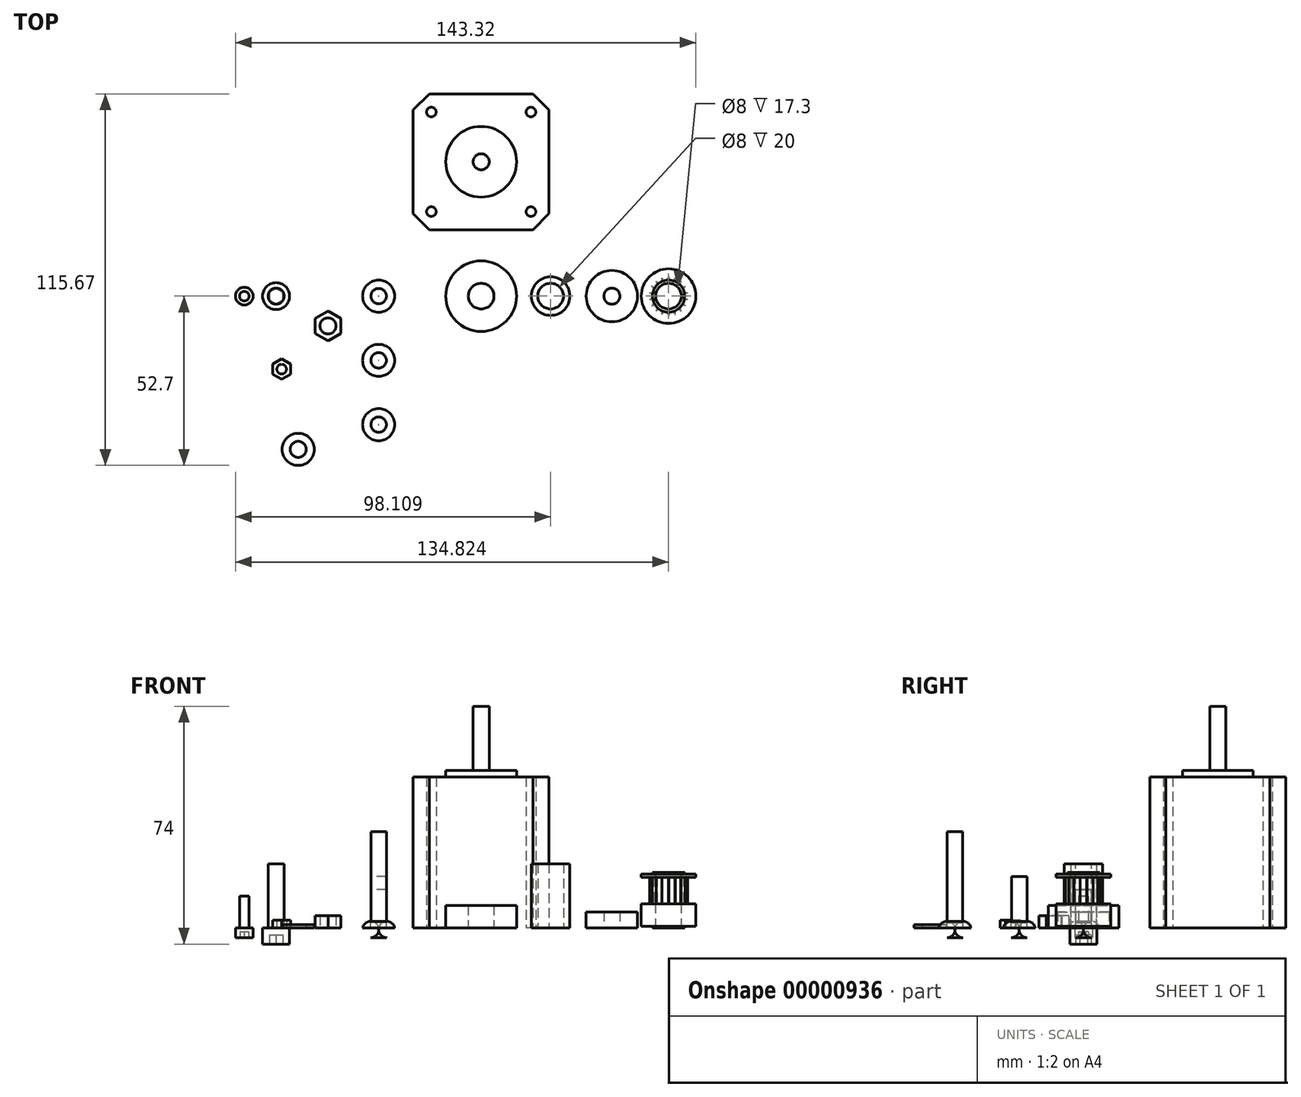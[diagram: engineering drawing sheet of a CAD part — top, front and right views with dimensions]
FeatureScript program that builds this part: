
annotation { "Feature Type Name" : "Feature", "Feature Type Description" : "" }
export const myFeature = defineFeature(function(context is Context, id is Id, definition is map)
    precondition{}
    {
        {
            var Q0;
            Q0=qCreatedBy(makeId("Top.planeOp"),FACE);
            var sketch = newSketch(context, id + "F0", { "sketchPlane" : qUnion([Q0])});
            skCircle(sketch, "E0", {"center": v(0, 0) * mm, "radius": 11 * mm});
            skCircle(sketch, "E1", {"center": v(0, 0) * mm, "radius": 4 * mm});
            skSolve(sketch);
        }
        {
            var Q0;
            Q0=makeQuery(id+"F0.imprint","IMPRINT",FACE,{"disambiguationData":[TD([[makeQuery(id+"F0.imprint","IMPRINT",EDGE,{"derivedFrom":sQuery(id+"F0.wireOp",EDGE,"E0")}),1.0]])]});
            extrude(context, id + "F1", {"entities" : qUnion([Q0]), "depth" : 7 * mm});
        }
        {
            var Q0;
            Q0=qCreatedBy(makeId("Top.planeOp"),FACE);
            var sketch = newSketch(context, id + "F2", { "sketchPlane" : qUnion([Q0])});
            skCircle(sketch, "E2.cCircle", {"center": v(-47.67, -9.27) * mm, "radius": 4 * mm, "construction": true});
            skLineSegment(sketch, "E2.0", {"start": v(-43.67, -6.96) * mm, "end": v(-43.67, -11.58) * mm});
            skLineSegment(sketch, "E2.1", {"start": v(-43.67, -11.58) * mm, "end": v(-47.67, -13.9) * mm});
            skLineSegment(sketch, "E2.2", {"start": v(-47.67, -13.9) * mm, "end": v(-51.67, -11.58) * mm});
            skLineSegment(sketch, "E2.3", {"start": v(-51.67, -11.58) * mm, "end": v(-51.67, -6.96) * mm});
            skLineSegment(sketch, "E2.4", {"start": v(-51.67, -6.96) * mm, "end": v(-47.67, -4.65) * mm});
            skLineSegment(sketch, "E2.5", {"start": v(-47.67, -4.65) * mm, "end": v(-43.67, -6.96) * mm});
            skPoint(sketch, "E2.0.midPoint", {"position": v(-43.67, -9.27) * mm});
            skCircle(sketch, "E3", {"center": v(-47.67, -9.27) * mm, "radius": 2.5 * mm});
            skSolve(sketch);
        }
        {
            var Q0;
            Q0=makeQuery(id+"F2.imprint","IMPRINT",FACE,{"disambiguationData":[TD([[makeQuery(id+"F2.imprint","IMPRINT",EDGE,{"derivedFrom":sQuery(id+"F2.wireOp",EDGE,"E2.0")}),-1.0]])]});
            extrude(context, id + "F3", {"entities" : qUnion([Q0]), "depth" : 3.8 * mm});
        }
        {
            var Q0;
            Q0=qCreatedBy(makeId("Front.planeOp"),FACE);
            var sketch = newSketch(context, id + "F4", { "sketchPlane" : qUnion([Q0])});
            skLineSegment(sketch, "E4", {"start": v(-36.9, 0) * mm, "end": v(-34.4, 0) * mm});
            skLineSegment(sketch, "E5", {"start": v(-34.4, 0) * mm, "end": v(-34.4, 1.7) * mm});
            skLineSegment(sketch, "E6", {"start": v(-34.3, 12) * mm, "end": v(-31.9, 12) * mm});
            skLineSegment(sketch, "E7", {"start": v(-31.9, 12) * mm, "end": v(-31.9, -3) * mm});
            skLineSegment(sketch, "E8", {"start": v(-31.9, -3) * mm, "end": v(-34.4, -3) * mm});
            skArc(sketch, "E9", {"start": v(-36.9, 0) * mm, "mid": v(-36.35, -2.09) * mm, "end": v(-34.4, -3) * mm});
            skLineSegment(sketch, "E10", {"start": v(-34.4, 1.7) * mm, "end": v(-34.3, 1.7) * mm});
            skLineSegment(sketch, "E11", {"start": v(-34.3, 1.7) * mm, "end": v(-34.3, 12) * mm});
            skSolve(sketch);
        }
        {
            var Q0;
            Q0=makeQuery(id+"F4.imprint","IMPRINT",FACE,{"disambiguationData":[TD([[makeQuery(id+"F4.imprint","IMPRINT",EDGE,{"derivedFrom":sQuery(id+"F4.wireOp",EDGE,"E4")}),-1.0]])]});
            var Q1;
            Q1=sQuery(id+"F4.wireOp",EDGE,"E7");
            revolve(context, id + "F5", {"entities" : qUnion([Q0]), "axis" : qUnion([Q1]), "revolveType" : RevolveType.FULL});
        }
        {
            var Q0;
            Q0=makeQuery(id+"F5.opRevolve","SWEPT_BODY",BODY,{"disambiguationData":[OSD([sQuery(id+"F4.wireOp",EDGE,"E4"),sQuery(id+"F4.wireOp",EDGE,"E5"),sQuery(id+"F4.wireOp",EDGE,"E6"),sQuery(id+"F4.wireOp",EDGE,"E7"),sQuery(id+"F4.wireOp",EDGE,"E8"),sQuery(id+"F4.wireOp",EDGE,"E9")])]});
            transform(context, id + "F6", {"entities" : qUnion([Q0]), "transformType" : TransformType.TRANSLATION_3D, "dx" : 0 * mm, "dy" : -(20 * mm), "dz" : 0 * mm, "makeCopy" : true});
        }
        {
            var Q0;
            Q0=makeQuery(id+"F6.opPattern","COPY",FACE,{"derivedFrom":makeQuery(id+"F5.opRevolve","SWEPT_FACE",FACE,{"disambiguationData":[OSD([sQuery(id+"F4.wireOp",EDGE,"E6")])]}),"instanceName":"1"});
            extrude(context, id + "F7", {"entities" : qUnion([Q0]), "operationType" : NewBodyOperationType.ADD, "depth" : 4 * mm});
        }
        {
            var Q0;
            Q0=qCreatedBy(makeId("Front.planeOp"),FACE);
            var sketch = newSketch(context, id + "F8", { "sketchPlane" : qUnion([Q0])});
            skLineSegment(sketch, "E12", {"start": v(-68.03, 0) * mm, "end": v(-66.33, 0) * mm});
            skLineSegment(sketch, "E13", {"start": v(-66.33, 0) * mm, "end": v(-66.33, 20) * mm});
            skLineSegment(sketch, "E14", {"start": v(-66.33, 20) * mm, "end": v(-63.83, 20) * mm});
            skLineSegment(sketch, "E15", {"start": v(-63.83, 20) * mm, "end": v(-63.83, -5) * mm});
            skLineSegment(sketch, "E16", {"start": v(-63.83, -5) * mm, "end": v(-68.03, -5) * mm});
            skLineSegment(sketch, "E17", {"start": v(-68.03, -5) * mm, "end": v(-68.03, 0) * mm});
            skSolve(sketch);
        }
        {
            var Q0;
            Q0=makeQuery(id+"F8.imprint","IMPRINT",FACE,{"disambiguationData":[TD([[makeQuery(id+"F8.imprint","IMPRINT",EDGE,{"derivedFrom":sQuery(id+"F8.wireOp",EDGE,"E12")}),-1.0]])]});
            var Q1;
            Q1=sQuery(id+"F8.wireOp",EDGE,"E15");
            revolve(context, id + "F9", {"entities" : qUnion([Q0]), "axis" : qUnion([Q1]), "revolveType" : RevolveType.FULL});
        }
        {
            var Q0;
            Q0=makeQuery(id+"F9.opRevolve","SWEPT_FACE",FACE,{"disambiguationData":[OSD([sQuery(id+"F8.wireOp",EDGE,"E16")])]});
            var sketch = newSketch(context, id + "F10", { "sketchPlane" : qUnion([Q0])});
            skCircle(sketch, "E18.cCircle", {"center": v(-63.83, 0) * mm, "radius": 2.06 * mm, "construction": true});
            skLineSegment(sketch, "E18.0", {"start": v(-61.77, 1.19) * mm, "end": v(-61.77, -1.19) * mm});
            skLineSegment(sketch, "E18.1", {"start": v(-61.77, -1.19) * mm, "end": v(-63.83, -2.38) * mm});
            skLineSegment(sketch, "E18.2", {"start": v(-63.83, -2.38) * mm, "end": v(-65.89, -1.19) * mm});
            skLineSegment(sketch, "E18.3", {"start": v(-65.89, -1.19) * mm, "end": v(-65.89, 1.19) * mm});
            skLineSegment(sketch, "E18.4", {"start": v(-65.89, 1.19) * mm, "end": v(-63.83, 2.38) * mm});
            skLineSegment(sketch, "E18.5", {"start": v(-63.83, 2.38) * mm, "end": v(-61.77, 1.19) * mm});
            skPoint(sketch, "E18.0.midPoint", {"position": v(-61.77, 0) * mm});
            skSolve(sketch);
        }
        {
            var Q0;
            Q0=makeQuery(id+"F10.imprint","IMPRINT",FACE,{"disambiguationData":[TD([[makeQuery(id+"F10.imprint","IMPRINT",EDGE,{"derivedFrom":sQuery(id+"F10.wireOp",EDGE,"E18.0")}),-1.0]])]});
            extrude(context, id + "F11", {"entities" : qUnion([Q0]), "operationType" : NewBodyOperationType.REMOVE, "oppositeDirection" : true, "depth" : 2.9 * mm});
        }
        {
            var Q0;
            Q0=qCreatedBy(makeId("Top.planeOp"),FACE);
            var sketch = newSketch(context, id + "F12", { "sketchPlane" : qUnion([Q0])});
            skCircle(sketch, "E19", {"center": v(21.62, 0) * mm, "radius": 4 * mm});
            skCircle(sketch, "E20", {"center": v(21.62, 0) * mm, "radius": 6 * mm});
            skSolve(sketch);
        }
        {
            var Q0;
            Q0=makeQuery(id+"F12.imprint","IMPRINT",FACE,{"disambiguationData":[TD([[makeQuery(id+"F12.imprint","IMPRINT",EDGE,{"derivedFrom":sQuery(id+"F12.wireOp",EDGE,"E19")}),-1.0]])]});
            extrude(context, id + "F13", {"entities" : qUnion([Q0]), "depth" : 20 * mm});
        }
        {
            var Q0;
            Q0=qCreatedBy(makeId("Top.planeOp"),FACE);
            var sketch = newSketch(context, id + "F14", { "sketchPlane" : qUnion([Q0])});
            skCircle(sketch, "E21", {"center": v(40.7, 0) * mm, "radius": 2.5 * mm});
            skCircle(sketch, "E22", {"center": v(40.7, 0) * mm, "radius": 8 * mm});
            skSolve(sketch);
        }
        {
            var Q0;
            Q0=makeQuery(id+"F14.imprint","IMPRINT",FACE,{"disambiguationData":[TD([[makeQuery(id+"F14.imprint","IMPRINT",EDGE,{"derivedFrom":sQuery(id+"F14.wireOp",EDGE,"E21")}),-1.0]])]});
            extrude(context, id + "F15", {"entities" : qUnion([Q0]), "depth" : 5 * mm});
        }
        {
            var Q0;
            Q0=qCreatedBy(makeId("Front.planeOp"),FACE);
            var sketch = newSketch(context, id + "F16", { "sketchPlane" : qUnion([Q0])});
            skLineSegment(sketch, "E23", {"start": v(54.33, 0) * mm, "end": v(54.33, 17.3) * mm});
            skLineSegment(sketch, "E24", {"start": v(54.33, 17.3) * mm, "end": v(53.33, 17.3) * mm});
            skLineSegment(sketch, "E25", {"start": v(53.33, 17.3) * mm, "end": v(53.33, 16.8) * mm});
            skLineSegment(sketch, "E26", {"start": v(53.33, 16.8) * mm, "end": v(49.83, 16.8) * mm});
            skLineSegment(sketch, "E27", {"start": v(49.83, 16.8) * mm, "end": v(49.83, 15.8) * mm});
            skLineSegment(sketch, "E28", {"start": v(49.83, 15.8) * mm, "end": v(52.33, 15.8) * mm});
            skLineSegment(sketch, "E29", {"start": v(52.33, 15.8) * mm, "end": v(52.33, 7.5) * mm});
            skLineSegment(sketch, "E30", {"start": v(52.33, 7.5) * mm, "end": v(49.83, 7.5) * mm});
            skLineSegment(sketch, "E31", {"start": v(49.83, 7.5) * mm, "end": v(49.83, 0.5) * mm});
            skLineSegment(sketch, "E32", {"start": v(49.83, 0.5) * mm, "end": v(53.33, 0.5) * mm});
            skLineSegment(sketch, "E33", {"start": v(53.33, 0.5) * mm, "end": v(53.33, 0) * mm});
            skLineSegment(sketch, "E34", {"start": v(53.33, 0) * mm, "end": v(54.33, 0) * mm});
            skLineSegment(sketch, "E35", {"start": v(58.33, 17.3) * mm, "end": v(58.33, 0) * mm, "construction": true});
            skSolve(sketch);
        }
        {
            var Q0;
            Q0=makeQuery(id+"F16.imprint","IMPRINT",FACE,{"disambiguationData":[TD([[makeQuery(id+"F16.imprint","IMPRINT",EDGE,{"derivedFrom":sQuery(id+"F16.wireOp",EDGE,"E23")}),1.0]])]});
            var Q1;
            Q1=sQuery(id+"F16.wireOp",EDGE,"E35");
            revolve(context, id + "F17", {"entities" : qUnion([Q0]), "axis" : qUnion([Q1]), "revolveType" : RevolveType.FULL});
        }
        {
            var Q0;
            Q0=qCreatedBy(makeId("Top.planeOp"),FACE);
            var sketch = newSketch(context, id + "F18", { "sketchPlane" : qUnion([Q0])});
            skLineSegment(sketch, "E36.rect.bottom", {"start": v(21.15, 20.67) * mm, "end": v(-21.15, 20.67) * mm});
            skLineSegment(sketch, "E36.rect.top", {"start": v(21.15, 62.97) * mm, "end": v(-21.15, 62.97) * mm});
            skLineSegment(sketch, "E36.rect.left", {"start": v(21.15, 20.67) * mm, "end": v(21.15, 62.97) * mm});
            skLineSegment(sketch, "E36.rect.right", {"start": v(-21.15, 20.67) * mm, "end": v(-21.15, 62.97) * mm});
            skPoint(sketch, "E36.rect.middle", {"position": v(0, 41.82) * mm});
            skCircle(sketch, "E37", {"center": v(0, 41.82) * mm, "radius": 11 * mm});
            skCircle(sketch, "E38", {"center": v(0, 41.82) * mm, "radius": 2.5 * mm});
            skLineSegment(sketch, "E39", {"start": v(-21.15, 57.97) * mm, "end": v(-16.15, 62.97) * mm});
            skLineSegment(sketch, "E40", {"start": v(16.15, 62.97) * mm, "end": v(21.15, 57.97) * mm});
            skLineSegment(sketch, "E41", {"start": v(21.15, 25.67) * mm, "end": v(16.15, 20.67) * mm});
            skLineSegment(sketch, "E42", {"start": v(-21.15, 25.67) * mm, "end": v(-16.15, 20.67) * mm});
            skLineSegment(sketch, "E43.rect.bottom", {"start": v(15.5, 57.32) * mm, "end": v(-15.5, 57.32) * mm, "construction": true});
            skLineSegment(sketch, "E43.rect.top", {"start": v(15.5, 26.32) * mm, "end": v(-15.5, 26.32) * mm, "construction": true});
            skLineSegment(sketch, "E43.rect.left", {"start": v(15.5, 57.32) * mm, "end": v(15.5, 26.32) * mm, "construction": true});
            skLineSegment(sketch, "E43.rect.right", {"start": v(-15.5, 57.32) * mm, "end": v(-15.5, 26.32) * mm, "construction": true});
            skCircle(sketch, "E44", {"center": v(-15.5, 57.32) * mm, "radius": 1.5 * mm});
            skCircle(sketch, "E45", {"center": v(15.5, 57.32) * mm, "radius": 1.5 * mm});
            skCircle(sketch, "E46", {"center": v(15.5, 26.32) * mm, "radius": 1.5 * mm});
            skCircle(sketch, "E47", {"center": v(-15.5, 26.32) * mm, "radius": 1.5 * mm});
            skSolve(sketch);
        }
        {
            var Q0;
            Q0=makeQuery(id+"F18.imprint","IMPRINT",FACE,{"disambiguationData":[TD([[makeQuery(id+"F18.imprint","IMPRINT",EDGE,{"derivedFrom":sQuery(id+"F18.wireOp",EDGE,"E37")}),-1.0]])]});
            extrude(context, id + "F19", {"entities" : qUnion([Q0]), "depth" : 47 * mm});
        }
        {
            var Q0;
            Q0=makeQuery(id+"F18.imprint","IMPRINT",FACE,{"disambiguationData":[TD([[makeQuery(id+"F18.imprint","IMPRINT",EDGE,{"derivedFrom":sQuery(id+"F18.wireOp",EDGE,"E37")}),1.0]])]});
            extrude(context, id + "F20", {"entities" : qUnion([Q0]), "operationType" : NewBodyOperationType.ADD, "depth" : 49 * mm});
        }
        {
            var Q0;
            Q0=makeQuery(id+"F18.imprint","IMPRINT",FACE,{"disambiguationData":[TD([[makeQuery(id+"F18.imprint","IMPRINT",EDGE,{"derivedFrom":sQuery(id+"F18.wireOp",EDGE,"E38")}),1.0]])]});
            extrude(context, id + "F21", {"entities" : qUnion([Q0]), "operationType" : NewBodyOperationType.ADD, "depth" : 69 * mm});
        }
        {
            var Q0;
            Q0=qCreatedBy(makeId("Top.planeOp"),FACE);
            var sketch = newSketch(context, id + "F22", { "sketchPlane" : qUnion([Q0])});
            skCircle(sketch, "E48", {"center": v(-62.1, -22.71) * mm, "radius": 1.5 * mm});
            skCircle(sketch, "E49.cCircle", {"center": v(-62.1, -22.71) * mm, "radius": 2.75 * mm, "construction": true});
            skLineSegment(sketch, "E49.0", {"start": v(-59.35, -21.12) * mm, "end": v(-59.35, -24.3) * mm});
            skLineSegment(sketch, "E49.1", {"start": v(-59.35, -24.3) * mm, "end": v(-62.1, -25.89) * mm});
            skLineSegment(sketch, "E49.2", {"start": v(-62.1, -25.89) * mm, "end": v(-64.85, -24.3) * mm});
            skLineSegment(sketch, "E49.3", {"start": v(-64.85, -24.3) * mm, "end": v(-64.85, -21.12) * mm});
            skLineSegment(sketch, "E49.4", {"start": v(-64.85, -21.12) * mm, "end": v(-62.1, -19.54) * mm});
            skLineSegment(sketch, "E49.5", {"start": v(-62.1, -19.54) * mm, "end": v(-59.35, -21.12) * mm});
            skPoint(sketch, "E49.0.midPoint", {"position": v(-59.35, -22.71) * mm});
            skSolve(sketch);
        }
        {
            var Q0;
            Q0=makeQuery(id+"F22.imprint","IMPRINT",FACE,{"disambiguationData":[TD([[makeQuery(id+"F22.imprint","IMPRINT",EDGE,{"derivedFrom":sQuery(id+"F22.wireOp",EDGE,"E48")}),-1.0]])]});
            extrude(context, id + "F23", {"entities" : qUnion([Q0]), "depth" : 2.4 * mm});
        }
        {
            var Q0;
            Q0=qCreatedBy(makeId("Front.planeOp"),FACE);
            var sketch = newSketch(context, id + "F24", { "sketchPlane" : qUnion([Q0])});
            skLineSegment(sketch, "E50", {"start": v(-75.24, 0) * mm, "end": v(-76.49, 0) * mm});
            skLineSegment(sketch, "E51", {"start": v(-76.49, 0) * mm, "end": v(-76.49, -3) * mm});
            skLineSegment(sketch, "E52", {"start": v(-76.49, -3) * mm, "end": v(-73.74, -3) * mm});
            skLineSegment(sketch, "E53", {"start": v(-73.74, -3) * mm, "end": v(-73.74, 10) * mm});
            skLineSegment(sketch, "E54", {"start": v(-73.74, 10) * mm, "end": v(-75.24, 10) * mm});
            skLineSegment(sketch, "E55", {"start": v(-75.24, 10) * mm, "end": v(-75.24, 0) * mm});
            skSolve(sketch);
        }
        {
            var Q0;
            Q0=makeQuery(id+"F24.imprint","IMPRINT",FACE,{"disambiguationData":[TD([[makeQuery(id+"F24.imprint","IMPRINT",EDGE,{"derivedFrom":sQuery(id+"F24.wireOp",EDGE,"E50")}),1.0]])]});
            var Q1;
            Q1=sQuery(id+"F24.wireOp",EDGE,"E53");
            revolve(context, id + "F25", {"entities" : qUnion([Q0]), "axis" : qUnion([Q1]), "revolveType" : RevolveType.FULL});
        }
        {
            var Q0;
            Q0=makeQuery(id+"F25.opRevolve","SWEPT_FACE",FACE,{"disambiguationData":[OSD([sQuery(id+"F24.wireOp",EDGE,"E52")])]});
            var sketch = newSketch(context, id + "F26", { "sketchPlane" : qUnion([Q0])});
            skCircle(sketch, "E56.cCircle", {"center": v(-73.74, 0) * mm, "radius": 1.3 * mm, "construction": true});
            skLineSegment(sketch, "E56.0", {"start": v(-72.44, 0.75) * mm, "end": v(-72.44, -0.75) * mm});
            skLineSegment(sketch, "E56.1", {"start": v(-72.44, -0.75) * mm, "end": v(-73.74, -1.5) * mm});
            skLineSegment(sketch, "E56.2", {"start": v(-73.74, -1.5) * mm, "end": v(-75.04, -0.75) * mm});
            skLineSegment(sketch, "E56.3", {"start": v(-75.04, -0.75) * mm, "end": v(-75.04, 0.75) * mm});
            skLineSegment(sketch, "E56.4", {"start": v(-75.04, 0.75) * mm, "end": v(-73.74, 1.5) * mm});
            skLineSegment(sketch, "E56.5", {"start": v(-73.74, 1.5) * mm, "end": v(-72.44, 0.75) * mm});
            skPoint(sketch, "E56.0.midPoint", {"position": v(-72.44, 0) * mm});
            skSolve(sketch);
        }
        {
            var Q0;
            Q0=makeQuery(id+"F26.imprint","IMPRINT",FACE,{"disambiguationData":[TD([[makeQuery(id+"F26.imprint","IMPRINT",EDGE,{"derivedFrom":sQuery(id+"F26.wireOp",EDGE,"E56.0")}),-1.0]])]});
            extrude(context, id + "F27", {"entities" : qUnion([Q0]), "operationType" : NewBodyOperationType.REMOVE, "oppositeDirection" : true, "depth" : 1.9 * mm});
        }
        {
            var Q0;
            Q0=makeQuery(id+"F17.opRevolve","SWEPT_FACE",FACE,{"disambiguationData":[OSD([sQuery(id+"F16.wireOp",EDGE,"E30")])]});
            var sketch = newSketch(context, id + "F28", { "sketchPlane" : qUnion([Q0])});
            skLineSegment(sketch, "E57.0", {"start": v(64.16, -0.98) * mm, "end": v(64.15, -1.07) * mm});
            skLineSegment(sketch, "E57.1", {"start": v(63.47, -2.92) * mm, "end": v(63.43, -3) * mm});
            skLineSegment(sketch, "E57.2", {"start": v(62.16, -4.5) * mm, "end": v(62.1, -4.55) * mm});
            skLineSegment(sketch, "E57.3", {"start": v(60.4, -5.54) * mm, "end": v(60.32, -5.57) * mm});
            skLineSegment(sketch, "E57.4", {"start": v(58.38, -5.9) * mm, "end": v(58.3, -5.9) * mm});
            skLineSegment(sketch, "E57.5", {"start": v(56.35, -5.57) * mm, "end": v(56.27, -5.54) * mm});
            skLineSegment(sketch, "E57.6", {"start": v(54.57, -4.55) * mm, "end": v(54.5, -4.5) * mm});
            skLineSegment(sketch, "E57.7", {"start": v(53.24, -3) * mm, "end": v(53.2, -2.92) * mm});
            skLineSegment(sketch, "E57.8", {"start": v(52.52, -1.07) * mm, "end": v(52.5, -0.98) * mm});
            skLineSegment(sketch, "E57.9", {"start": v(52.5, 0.98) * mm, "end": v(52.52, 1.07) * mm});
            skLineSegment(sketch, "E57.10", {"start": v(53.2, 2.92) * mm, "end": v(53.24, 3) * mm});
            skLineSegment(sketch, "E57.11", {"start": v(54.5, 4.5) * mm, "end": v(54.57, 4.55) * mm});
            skLineSegment(sketch, "E57.12", {"start": v(56.27, 5.54) * mm, "end": v(56.35, 5.57) * mm});
            skLineSegment(sketch, "E57.13", {"start": v(58.3, 5.9) * mm, "end": v(58.38, 5.9) * mm});
            skLineSegment(sketch, "E57.14", {"start": v(60.32, 5.57) * mm, "end": v(60.4, 5.54) * mm});
            skLineSegment(sketch, "E57.15", {"start": v(62.1, 4.55) * mm, "end": v(62.16, 4.5) * mm});
            skLineSegment(sketch, "E57.16", {"start": v(63.43, 3) * mm, "end": v(63.47, 2.92) * mm});
            skLineSegment(sketch, "E57.17", {"start": v(64.15, 1.07) * mm, "end": v(64.16, 0.98) * mm});
            skCircle(sketch, "E58", {"center": v(55.33, -5.2) * mm, "radius": 1 * mm});
            skCircle(sketch, "E59", {"center": v(53.74, -3.86) * mm, "radius": 1 * mm});
            skCircle(sketch, "E60", {"center": v(52.7, -2.05) * mm, "radius": 1 * mm});
            skCircle(sketch, "E61", {"center": v(52.33, 0) * mm, "radius": 1 * mm});
            skCircle(sketch, "E62", {"center": v(52.7, 2.05) * mm, "radius": 1 * mm});
            skCircle(sketch, "E63", {"center": v(57.3, -5.9) * mm, "radius": 1 * mm});
            skCircle(sketch, "E64", {"center": v(59.38, -5.9) * mm, "radius": 1 * mm});
            skCircle(sketch, "E65", {"center": v(61.33, -5.2) * mm, "radius": 1 * mm});
            skCircle(sketch, "E66", {"center": v(62.93, -3.86) * mm, "radius": 1 * mm});
            skCircle(sketch, "E67", {"center": v(63.97, -2.05) * mm, "radius": 1 * mm});
            skCircle(sketch, "E68", {"center": v(64.33, 0) * mm, "radius": 1 * mm});
            skCircle(sketch, "E69", {"center": v(63.97, 2.05) * mm, "radius": 1 * mm});
            skCircle(sketch, "E70", {"center": v(62.93, 3.86) * mm, "radius": 1 * mm});
            skCircle(sketch, "E71", {"center": v(61.33, 5.2) * mm, "radius": 1 * mm});
            skCircle(sketch, "E72", {"center": v(59.38, 5.9) * mm, "radius": 1 * mm});
            skCircle(sketch, "E73", {"center": v(57.3, 5.9) * mm, "radius": 1 * mm});
            skCircle(sketch, "E74", {"center": v(55.33, 5.2) * mm, "radius": 1 * mm});
            skCircle(sketch, "E75", {"center": v(53.74, 3.86) * mm, "radius": 1 * mm});
            skSolve(sketch);
        }
        {
            var Q0;
            {var subQ0=sQuery(id+"F28.wireOp",EDGE,"E62");var subQ2=makeQuery(id+"F28.imprint","INTERSECT",VERTEX,{"derivedFrom":[sQuery(id+"F28.wireOp",EDGE,"E57.9"),subQ0]});Q0=makeQuery(id+"F28.imprint","IMPRINT",FACE,{"disambiguationData":[TD([[makeQuery(id+"F28.imprint","IMPRINT",EDGE,{"disambiguationData":[TD([[subQ2,-1.0]])],"derivedFrom":subQ0}),1.0]])]});}
            var Q1;
            {var subQ1=sQuery(id+"F28.wireOp",EDGE,"E61");var subQ5=makeQuery(id+"F28.imprint","INTERSECT",VERTEX,{"derivedFrom":[sQuery(id+"F28.wireOp",EDGE,"E57.8"),subQ1]});Q1=makeQuery(id+"F28.imprint","IMPRINT",FACE,{"disambiguationData":[TD([[makeQuery(id+"F28.imprint","IMPRINT",EDGE,{"disambiguationData":[TD([[subQ5,-1.0]])],"derivedFrom":subQ1}),1.0]])]});}
            var Q2;
            {var subQ1=sQuery(id+"F28.wireOp",EDGE,"E60");var subQ5=makeQuery(id+"F28.imprint","INTERSECT",VERTEX,{"derivedFrom":[sQuery(id+"F28.wireOp",EDGE,"E57.7"),subQ1]});Q2=makeQuery(id+"F28.imprint","IMPRINT",FACE,{"disambiguationData":[TD([[makeQuery(id+"F28.imprint","IMPRINT",EDGE,{"disambiguationData":[TD([[subQ5,-1.0]])],"derivedFrom":subQ1}),1.0]])]});}
            var Q3;
            {var subQ1=sQuery(id+"F28.wireOp",EDGE,"E59");var subQ5=makeQuery(id+"F28.imprint","INTERSECT",VERTEX,{"derivedFrom":[sQuery(id+"F28.wireOp",EDGE,"E57.6"),subQ1]});Q3=makeQuery(id+"F28.imprint","IMPRINT",FACE,{"disambiguationData":[TD([[makeQuery(id+"F28.imprint","IMPRINT",EDGE,{"disambiguationData":[TD([[subQ5,-1.0]])],"derivedFrom":subQ1}),1.0]])]});}
            var Q4;
            {var subQ1=sQuery(id+"F28.wireOp",EDGE,"E58");var subQ5=makeQuery(id+"F28.imprint","INTERSECT",VERTEX,{"derivedFrom":[sQuery(id+"F28.wireOp",EDGE,"E57.5"),subQ1]});Q4=makeQuery(id+"F28.imprint","IMPRINT",FACE,{"disambiguationData":[TD([[makeQuery(id+"F28.imprint","IMPRINT",EDGE,{"disambiguationData":[TD([[subQ5,-1.0]])],"derivedFrom":subQ1}),1.0]])]});}
            var Q5;
            {var subQ1=sQuery(id+"F28.wireOp",EDGE,"E63");var subQ4=makeQuery(id+"F28.imprint","INTERSECT",VERTEX,{"derivedFrom":[sQuery(id+"F28.wireOp",EDGE,"E57.4"),subQ1]});Q5=makeQuery(id+"F28.imprint","IMPRINT",FACE,{"disambiguationData":[TD([[makeQuery(id+"F28.imprint","IMPRINT",EDGE,{"disambiguationData":[TD([[subQ4,-1.0]])],"derivedFrom":subQ1}),1.0]])]});}
            var Q6;
            {var subQ1=sQuery(id+"F28.wireOp",EDGE,"E64");var subQ5=makeQuery(id+"F28.imprint","INTERSECT",VERTEX,{"derivedFrom":[sQuery(id+"F28.wireOp",EDGE,"E57.3"),subQ1]});Q6=makeQuery(id+"F28.imprint","IMPRINT",FACE,{"disambiguationData":[TD([[makeQuery(id+"F28.imprint","IMPRINT",EDGE,{"disambiguationData":[TD([[subQ5,-1.0]])],"derivedFrom":subQ1}),1.0]])]});}
            var Q7;
            {var subQ0=sQuery(id+"F28.wireOp",EDGE,"E65");var subQ5=makeQuery(id+"F28.imprint","INTERSECT",VERTEX,{"derivedFrom":[sQuery(id+"F28.wireOp",EDGE,"E57.2"),subQ0]});Q7=makeQuery(id+"F28.imprint","IMPRINT",FACE,{"disambiguationData":[TD([[makeQuery(id+"F28.imprint","IMPRINT",EDGE,{"disambiguationData":[TD([[subQ5,-1.0]])],"derivedFrom":subQ0}),1.0]])]});}
            var Q8;
            {var subQ1=sQuery(id+"F28.wireOp",EDGE,"E66");var subQ5=makeQuery(id+"F28.imprint","INTERSECT",VERTEX,{"derivedFrom":[sQuery(id+"F28.wireOp",EDGE,"E57.1"),subQ1]});Q8=makeQuery(id+"F28.imprint","IMPRINT",FACE,{"disambiguationData":[TD([[makeQuery(id+"F28.imprint","IMPRINT",EDGE,{"disambiguationData":[TD([[subQ5,-1.0]])],"derivedFrom":subQ1}),1.0]])]});}
            var Q9;
            {var subQ1=sQuery(id+"F28.wireOp",EDGE,"E67");var subQ5=makeQuery(id+"F28.imprint","INTERSECT",VERTEX,{"derivedFrom":[sQuery(id+"F28.wireOp",EDGE,"E57.0"),subQ1]});Q9=makeQuery(id+"F28.imprint","IMPRINT",FACE,{"disambiguationData":[TD([[makeQuery(id+"F28.imprint","IMPRINT",EDGE,{"disambiguationData":[TD([[subQ5,-1.0]])],"derivedFrom":subQ1}),1.0]])]});}
            var Q10;
            {var subQ0=sQuery(id+"F28.wireOp",EDGE,"E68");var subQ3=makeQuery(id+"F28.imprint","INTERSECT",VERTEX,{"derivedFrom":[sQuery(id+"F28.wireOp",EDGE,"E57.0"),subQ0]});Q10=makeQuery(id+"F28.imprint","IMPRINT",FACE,{"disambiguationData":[TD([[makeQuery(id+"F28.imprint","IMPRINT",EDGE,{"disambiguationData":[TD([[subQ3,1.0]])],"derivedFrom":subQ0}),1.0]])]});}
            var Q11;
            {var subQ1=sQuery(id+"F28.wireOp",EDGE,"E69");var subQ5=makeQuery(id+"F28.imprint","INTERSECT",VERTEX,{"derivedFrom":[sQuery(id+"F28.wireOp",EDGE,"E57.16"),subQ1]});Q11=makeQuery(id+"F28.imprint","IMPRINT",FACE,{"disambiguationData":[TD([[makeQuery(id+"F28.imprint","IMPRINT",EDGE,{"disambiguationData":[TD([[subQ5,-1.0]])],"derivedFrom":subQ1}),1.0]])]});}
            var Q12;
            {var subQ1=sQuery(id+"F28.wireOp",EDGE,"E70");var subQ5=makeQuery(id+"F28.imprint","INTERSECT",VERTEX,{"derivedFrom":[sQuery(id+"F28.wireOp",EDGE,"E57.15"),subQ1]});Q12=makeQuery(id+"F28.imprint","IMPRINT",FACE,{"disambiguationData":[TD([[makeQuery(id+"F28.imprint","IMPRINT",EDGE,{"disambiguationData":[TD([[subQ5,-1.0]])],"derivedFrom":subQ1}),1.0]])]});}
            var Q13;
            {var subQ1=sQuery(id+"F28.wireOp",EDGE,"E71");var subQ5=makeQuery(id+"F28.imprint","INTERSECT",VERTEX,{"derivedFrom":[sQuery(id+"F28.wireOp",EDGE,"E57.14"),subQ1]});Q13=makeQuery(id+"F28.imprint","IMPRINT",FACE,{"disambiguationData":[TD([[makeQuery(id+"F28.imprint","IMPRINT",EDGE,{"disambiguationData":[TD([[subQ5,-1.0]])],"derivedFrom":subQ1}),1.0]])]});}
            var Q14;
            {var subQ1=sQuery(id+"F28.wireOp",EDGE,"E72");var subQ5=makeQuery(id+"F28.imprint","INTERSECT",VERTEX,{"derivedFrom":[sQuery(id+"F28.wireOp",EDGE,"E57.13"),subQ1]});Q14=makeQuery(id+"F28.imprint","IMPRINT",FACE,{"disambiguationData":[TD([[makeQuery(id+"F28.imprint","IMPRINT",EDGE,{"disambiguationData":[TD([[subQ5,-1.0]])],"derivedFrom":subQ1}),1.0]])]});}
            var Q15;
            {var subQ1=sQuery(id+"F28.wireOp",EDGE,"E73");var subQ5=makeQuery(id+"F28.imprint","INTERSECT",VERTEX,{"derivedFrom":[sQuery(id+"F28.wireOp",EDGE,"E57.12"),subQ1]});Q15=makeQuery(id+"F28.imprint","IMPRINT",FACE,{"disambiguationData":[TD([[makeQuery(id+"F28.imprint","IMPRINT",EDGE,{"disambiguationData":[TD([[subQ5,-1.0]])],"derivedFrom":subQ1}),1.0]])]});}
            var Q16;
            {var subQ0=sQuery(id+"F28.wireOp",EDGE,"E74");var subQ2=makeQuery(id+"F28.imprint","INTERSECT",VERTEX,{"derivedFrom":[sQuery(id+"F28.wireOp",EDGE,"E57.11"),subQ0]});Q16=makeQuery(id+"F28.imprint","IMPRINT",FACE,{"disambiguationData":[TD([[makeQuery(id+"F28.imprint","IMPRINT",EDGE,{"disambiguationData":[TD([[subQ2,-1.0]])],"derivedFrom":subQ0}),1.0]])]});}
            var Q17;
            {var subQ0=sQuery(id+"F28.wireOp",EDGE,"E75");var subQ2=makeQuery(id+"F28.imprint","INTERSECT",VERTEX,{"derivedFrom":[sQuery(id+"F28.wireOp",EDGE,"E57.10"),subQ0]});Q17=makeQuery(id+"F28.imprint","IMPRINT",FACE,{"disambiguationData":[TD([[makeQuery(id+"F28.imprint","IMPRINT",EDGE,{"disambiguationData":[TD([[subQ2,-1.0]])],"derivedFrom":subQ0}),1.0]])]});}
            extrude(context, id + "F29", {"entities" : qUnion([Q0, Q1, Q2, Q3, Q4, Q5, Q6, Q7, Q8, Q9, Q10, Q11, Q12, Q13, Q14, Q15, Q16, Q17]), "operationType" : NewBodyOperationType.REMOVE, "depth" : 8.3 * mm});
        }
        {
            var Q0;
            Q0=makeQuery(id+"F5.opRevolve","SWEPT_BODY",BODY,{"disambiguationData":[OSD([sQuery(id+"F4.wireOp",EDGE,"E4"),sQuery(id+"F4.wireOp",EDGE,"E5"),sQuery(id+"F4.wireOp",EDGE,"E6"),sQuery(id+"F4.wireOp",EDGE,"E7"),sQuery(id+"F4.wireOp",EDGE,"E8"),sQuery(id+"F4.wireOp",EDGE,"E9"),sQuery(id+"F4.wireOp",EDGE,"E10"),sQuery(id+"F4.wireOp",EDGE,"E11")])]});
            transform(context, id + "F30", {"entities" : qUnion([Q0]), "transformType" : TransformType.TRANSLATION_3D, "dx" : 0 * mm, "dy" : -(40 * mm), "dz" : 0 * mm, "makeCopy" : true});
        }
        {
            var Q0;
            Q0=makeQuery(id+"F30.opPattern","COPY",FACE,{"derivedFrom":makeQuery(id+"F5.opRevolve","SWEPT_FACE",FACE,{"disambiguationData":[OSD([sQuery(id+"F4.wireOp",EDGE,"E6")])]}),"instanceName":"1"});
            extrude(context, id + "F31", {"entities" : qUnion([Q0]), "operationType" : NewBodyOperationType.ADD, "depth" : 18 * mm});
        }
        {
            var Q0;
            Q0=qCreatedBy(makeId("Top.planeOp"),FACE);
            var sketch = newSketch(context, id + "F32", { "sketchPlane" : qUnion([Q0])});
            skCircle(sketch, "E76", {"center": v(-56.95, -47.7) * mm, "radius": 2.5 * mm});
            skCircle(sketch, "E77", {"center": v(-56.95, -47.7) * mm, "radius": 5 * mm});
            skSolve(sketch);
        }
        {
            var Q0;
            Q0=makeQuery(id+"F32.imprint","IMPRINT",FACE,{"disambiguationData":[TD([[makeQuery(id+"F32.imprint","IMPRINT",EDGE,{"derivedFrom":sQuery(id+"F32.wireOp",EDGE,"E76")}),-1.0]])]});
            extrude(context, id + "F33", {"entities" : qUnion([Q0]), "depth" : 1 * mm});
        }
    });
